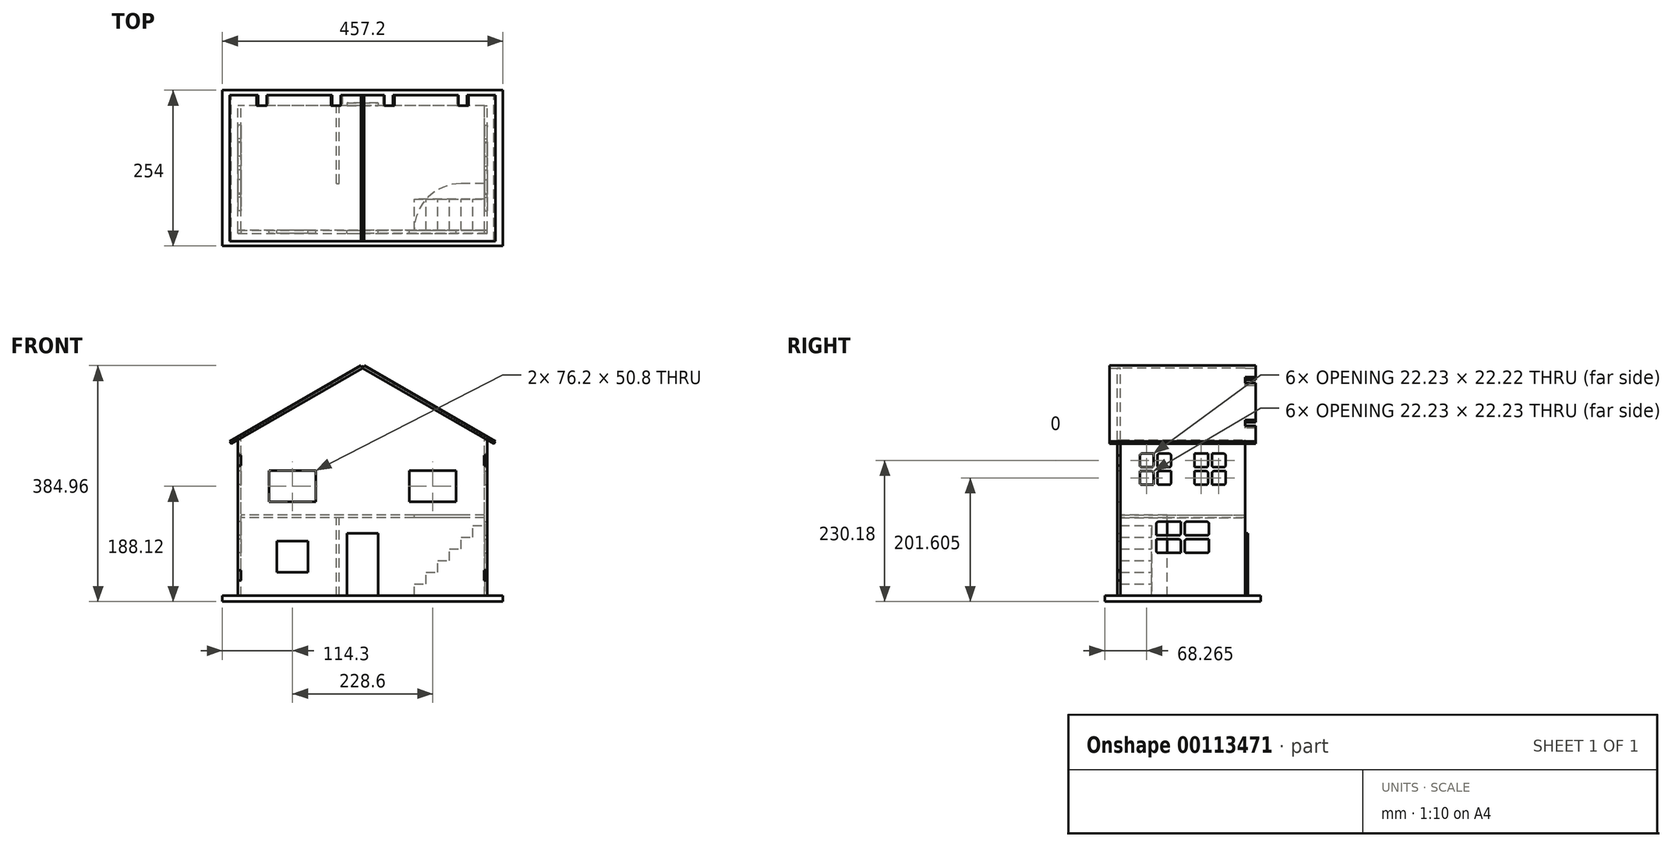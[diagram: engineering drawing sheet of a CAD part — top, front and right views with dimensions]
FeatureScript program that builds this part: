
annotation { "Feature Type Name" : "Feature", "Feature Type Description" : "" }
export const myFeature = defineFeature(function(context is Context, id is Id, definition is map)
    precondition{}
    {
        {
            var Q0;
            Q0=qCreatedBy(makeId("Front.planeOp"),FACE);
            var sketch = newSketch(context, id + "F0", { "sketchPlane" : qUnion([Q0])});
            skLineSegment(sketch, "E0.bottom", {"start": v(-25.4, 0) * mm, "end": v(25.4, 0) * mm});
            skLineSegment(sketch, "E0.top", {"start": v(-25.4, 101.6) * mm, "end": v(25.4, 101.6) * mm});
            skLineSegment(sketch, "E0.left", {"start": v(-25.4, 0) * mm, "end": v(-25.4, 101.6) * mm});
            skLineSegment(sketch, "E0.right", {"start": v(25.4, 0) * mm, "end": v(25.4, 101.6) * mm});
            skLineSegment(sketch, "E1", {"start": v(0, 0) * mm, "end": v(0, -53.95) * mm, "construction": true});
            skLineSegment(sketch, "E2", {"start": v(-203.2, 0) * mm, "end": v(-203.2, 254) * mm});
            skLineSegment(sketch, "E3", {"start": v(-203.2, 254) * mm, "end": v(0, 371.32) * mm});
            skLineSegment(sketch, "E4.MirrorCS", {"start": v(203.2, 0) * mm, "end": v(203.2, 254) * mm});
            skLineSegment(sketch, "E5.MirrorCS", {"start": v(203.2, 254) * mm, "end": v(0, 371.32) * mm});
            skLineSegment(sketch, "E6", {"start": v(-203.2, 0) * mm, "end": v(-25.4, 0) * mm});
            skLineSegment(sketch, "E7", {"start": v(25.4, 0) * mm, "end": v(203.2, 0) * mm});
            skLineSegment(sketch, "E8.bottom", {"start": v(-88.9, 38.1) * mm, "end": v(-139.7, 38.1) * mm});
            skLineSegment(sketch, "E8.top", {"start": v(-88.9, 88.9) * mm, "end": v(-139.7, 88.9) * mm});
            skLineSegment(sketch, "E8.left", {"start": v(-88.9, 38.1) * mm, "end": v(-88.9, 88.9) * mm});
            skLineSegment(sketch, "E8.right", {"start": v(-139.7, 38.1) * mm, "end": v(-139.7, 88.9) * mm});
            skPoint(sketch, "E8.middle", {"position": v(-114.3, 63.5) * mm});
            skLineSegment(sketch, "E9", {"start": v(0, 371.32) * mm, "end": v(-61.92, 371.32) * mm, "construction": true});
            skLineSegment(sketch, "E10.bottom", {"start": v(76.2, 204) * mm, "end": v(152.4, 204) * mm});
            skLineSegment(sketch, "E10.top", {"start": v(76.2, 153.2) * mm, "end": v(152.4, 153.2) * mm});
            skLineSegment(sketch, "E10.left", {"start": v(76.2, 204) * mm, "end": v(76.2, 153.2) * mm});
            skLineSegment(sketch, "E10.right", {"start": v(152.4, 204) * mm, "end": v(152.4, 153.2) * mm});
            skPoint(sketch, "E10.middle", {"position": v(114.3, 178.6) * mm});
            skPoint(sketch, "E11.MirrorP", {"position": v(-114.3, 178.6) * mm});
            skLineSegment(sketch, "E12.MirrorCS", {"start": v(-152.4, 204) * mm, "end": v(-152.4, 153.2) * mm});
            skLineSegment(sketch, "E13.MirrorCS", {"start": v(-76.2, 204) * mm, "end": v(-76.2, 153.2) * mm});
            skLineSegment(sketch, "E14.MirrorCS", {"start": v(-76.2, 153.2) * mm, "end": v(-152.4, 153.2) * mm});
            skLineSegment(sketch, "E15.MirrorCS", {"start": v(-76.2, 204) * mm, "end": v(-152.4, 204) * mm});
            skSolve(sketch);
        }
        {
            var Q0;
            Q0=makeQuery(id+"F0.imprint","IMPRINT",FACE,{"disambiguationData":[TD([[makeQuery(id+"F0.imprint","IMPRINT",EDGE,{"derivedFrom":sQuery(id+"F0.wireOp",EDGE,"E0.top")}),1.0]])]});
            extrude(context, id + "F1", {"entities" : qUnion([Q0]), "depth" : 4.76 * mm});
        }
        {
            var Q0;
            Q0=makeQuery(id+"F1.opExtrude","SWEPT_FACE",FACE,{"disambiguationData":[OSD([sQuery(id+"F0.wireOp",EDGE,"E2")])]});
            var sketch = newSketch(context, id + "F2", { "sketchPlane" : qUnion([Q0])});
            skLineSegment(sketch, "E16.bottom", {"start": v(0, 0) * mm, "end": v(-203.2, 0) * mm});
            skLineSegment(sketch, "E16.top", {"start": v(0, 254) * mm, "end": v(-203.2, 254) * mm});
            skLineSegment(sketch, "E16.left", {"start": v(0, 0) * mm, "end": v(0, 25.4) * mm});
            skLineSegment(sketch, "E16.right", {"start": v(-203.2, 0) * mm, "end": v(-203.2, 25.4) * mm});
            skLineSegment(sketch, "E17.bottom", {"start": v(-144.46, 120.65) * mm, "end": v(-58.74, 120.65) * mm});
            skLineSegment(sketch, "E17.top", {"start": v(-144.46, 69.85) * mm, "end": v(-58.74, 69.85) * mm});
            skLineSegment(sketch, "E17.left", {"start": v(-144.46, 120.65) * mm, "end": v(-144.46, 69.85) * mm});
            skLineSegment(sketch, "E17.right", {"start": v(-58.74, 120.65) * mm, "end": v(-58.74, 69.85) * mm});
            skLineSegment(sketch, "E18", {"start": v(-101.6, 120.65) * mm, "end": v(-101.6, 254) * mm, "construction": true});
            skLineSegment(sketch, "E19.bottom", {"start": v(-120.65, 231.77) * mm, "end": v(-171.45, 231.77) * mm});
            skLineSegment(sketch, "E19.top", {"start": v(-120.65, 180.97) * mm, "end": v(-171.45, 180.97) * mm});
            skLineSegment(sketch, "E19.left", {"start": v(-120.65, 231.77) * mm, "end": v(-120.65, 180.97) * mm});
            skLineSegment(sketch, "E19.right", {"start": v(-171.45, 231.77) * mm, "end": v(-171.45, 180.97) * mm});
            skPoint(sketch, "E19.middle", {"position": v(-146.05, 206.37) * mm});
            skLineSegment(sketch, "E20.MirrorCS", {"start": v(-31.75, 231.77) * mm, "end": v(-31.75, 180.97) * mm});
            skLineSegment(sketch, "E21.MirrorCS", {"start": v(-82.55, 180.97) * mm, "end": v(-31.75, 180.97) * mm});
            skLineSegment(sketch, "E22.MirrorCS", {"start": v(-82.55, 231.77) * mm, "end": v(-82.55, 180.97) * mm});
            skLineSegment(sketch, "E23.MirrorCS", {"start": v(-82.55, 231.77) * mm, "end": v(-31.75, 231.77) * mm});
            skLineSegment(sketch, "E24", {"start": v(-149.22, 231.77) * mm, "end": v(-149.22, 209.55) * mm});
            skLineSegment(sketch, "E25", {"start": v(-149.22, 209.55) * mm, "end": v(-171.45, 209.55) * mm});
            skLineSegment(sketch, "E26", {"start": v(-171.45, 206.37) * mm, "end": v(-146.05, 206.37) * mm, "construction": true});
            skLineSegment(sketch, "E27", {"start": v(-146.05, 206.37) * mm, "end": v(-146.05, 231.77) * mm, "construction": true});
            skLineSegment(sketch, "E28.MirrorCS", {"start": v(-142.88, 209.55) * mm, "end": v(-120.65, 209.55) * mm});
            skLineSegment(sketch, "E29.MirrorCS", {"start": v(-142.88, 231.77) * mm, "end": v(-142.88, 209.55) * mm});
            skLineSegment(sketch, "E30.MirrorCS", {"start": v(-149.22, 203.2) * mm, "end": v(-171.45, 203.2) * mm});
            skLineSegment(sketch, "E31.MirrorCS", {"start": v(-149.22, 180.97) * mm, "end": v(-149.22, 203.2) * mm});
            skLineSegment(sketch, "E32.MirrorCS", {"start": v(-142.88, 180.97) * mm, "end": v(-142.88, 203.2) * mm});
            skLineSegment(sketch, "E33.MirrorCS", {"start": v(-142.88, 203.2) * mm, "end": v(-120.65, 203.2) * mm});
            skLineSegment(sketch, "E34.MirrorCS", {"start": v(-60.33, 231.77) * mm, "end": v(-60.33, 209.55) * mm});
            skLineSegment(sketch, "E35.MirrorCS", {"start": v(-60.33, 203.2) * mm, "end": v(-82.55, 203.2) * mm});
            skLineSegment(sketch, "E36.MirrorCS", {"start": v(-53.98, 231.77) * mm, "end": v(-53.98, 209.55) * mm});
            skLineSegment(sketch, "E37.MirrorCS", {"start": v(-53.98, 209.55) * mm, "end": v(-31.75, 209.55) * mm});
            skLineSegment(sketch, "E38.MirrorCS", {"start": v(-53.98, 203.2) * mm, "end": v(-31.75, 203.2) * mm});
            skLineSegment(sketch, "E39.MirrorCS", {"start": v(-53.98, 180.97) * mm, "end": v(-53.98, 203.2) * mm});
            skLineSegment(sketch, "E40.MirrorCS", {"start": v(-60.33, 209.55) * mm, "end": v(-82.55, 209.55) * mm});
            skLineSegment(sketch, "E41.MirrorCS", {"start": v(-60.33, 180.97) * mm, "end": v(-60.33, 203.2) * mm});
            skLineSegment(sketch, "E42", {"start": v(-104.77, 120.65) * mm, "end": v(-104.77, 98.43) * mm});
            skLineSegment(sketch, "E43", {"start": v(-104.77, 98.43) * mm, "end": v(-144.46, 98.43) * mm});
            skLineSegment(sketch, "E44.MirrorCS", {"start": v(-98.42, 120.65) * mm, "end": v(-98.42, 98.43) * mm});
            skLineSegment(sketch, "E45.MirrorCS", {"start": v(-98.42, 98.43) * mm, "end": v(-58.74, 98.43) * mm});
            skLineSegment(sketch, "E46", {"start": v(-119.08, 95.25) * mm, "end": v(-144.46, 95.25) * mm, "construction": true});
            skLineSegment(sketch, "E47.MirrorCS", {"start": v(-104.77, 92.08) * mm, "end": v(-144.46, 92.08) * mm});
            skLineSegment(sketch, "E48.MirrorCS", {"start": v(-104.77, 69.85) * mm, "end": v(-104.77, 92.08) * mm});
            skLineSegment(sketch, "E49.MirrorCS", {"start": v(-98.42, 69.85) * mm, "end": v(-98.42, 92.08) * mm});
            skLineSegment(sketch, "E50.MirrorCS", {"start": v(-98.42, 92.08) * mm, "end": v(-58.74, 92.08) * mm});
            skLineSegment(sketch, "E51", {"start": v(0, 228.6) * mm, "end": v(4.76, 228.6) * mm});
            skLineSegment(sketch, "E52", {"start": v(4.76, 228.6) * mm, "end": v(4.76, 212.72) * mm});
            skLineSegment(sketch, "E53", {"start": v(4.76, 212.73) * mm, "end": v(0, 212.73) * mm});
            skLineSegment(sketch, "E54", {"start": v(0, 127) * mm, "end": v(28.62, 127) * mm, "construction": true});
            skLineSegment(sketch, "E55.MirrorCS", {"start": v(0, 25.4) * mm, "end": v(4.76, 25.4) * mm});
            skLineSegment(sketch, "E56.MirrorCS", {"start": v(4.76, 25.4) * mm, "end": v(4.76, 41.28) * mm});
            skLineSegment(sketch, "E57.MirrorCS", {"start": v(4.76, 41.27) * mm, "end": v(0, 41.27) * mm});
            skLineSegment(sketch, "E58.trimOffspring", {"start": v(0, 41.27) * mm, "end": v(0, 212.73) * mm});
            skLineSegment(sketch, "E59.trimOffspring", {"start": v(0, 228.6) * mm, "end": v(0, 254) * mm});
            skLineSegment(sketch, "E60.MirrorCS", {"start": v(-207.96, 212.72) * mm, "end": v(-203.2, 212.72) * mm});
            skLineSegment(sketch, "E61.MirrorCS", {"start": v(-207.96, 228.6) * mm, "end": v(-207.96, 212.72) * mm});
            skLineSegment(sketch, "E62.MirrorCS", {"start": v(-203.2, 228.6) * mm, "end": v(-207.96, 228.6) * mm});
            skLineSegment(sketch, "E63.MirrorCS", {"start": v(-203.2, 25.4) * mm, "end": v(-207.96, 25.4) * mm});
            skLineSegment(sketch, "E64.MirrorCS", {"start": v(-207.96, 25.4) * mm, "end": v(-207.96, 41.27) * mm});
            skLineSegment(sketch, "E65.MirrorCS", {"start": v(-207.96, 41.27) * mm, "end": v(-203.2, 41.27) * mm});
            skLineSegment(sketch, "E66.trimOffspring", {"start": v(-203.2, 41.27) * mm, "end": v(-203.2, 212.72) * mm});
            skLineSegment(sketch, "E67.trimOffspring", {"start": v(-203.2, 228.6) * mm, "end": v(-203.2, 254) * mm});
            skSolve(sketch);
        }
        {
            var Q0;
            Q0 = qSketchRegion(id + "F2", true);
            extrude(context, id + "F3", {"entities" : qUnion([Q0]), "oppositeDirection" : true, "depth" : 4.76 * mm});
        }
        {
            var Q0;
            {var subQ6=sQuery(id+"F2.wireOp",EDGE,"E24");Q0=makeQuery(id+"F2.imprint","IMPRINT",FACE,{"disambiguationData":[TD([[makeQuery(id+"F2.imprint","IMPRINT",EDGE,{"derivedFrom":subQ6}),1.0]])]});}
            var Q1;
            {var subQ5=sQuery(id+"F2.wireOp",EDGE,"E34.MirrorCS");Q1=makeQuery(id+"F2.imprint","IMPRINT",FACE,{"disambiguationData":[TD([[makeQuery(id+"F2.imprint","IMPRINT",EDGE,{"derivedFrom":subQ5}),1.0]])]});}
            var Q2;
            {var subQ5=sQuery(id+"F2.wireOp",EDGE,"E42");Q2=makeQuery(id+"F2.imprint","IMPRINT",FACE,{"disambiguationData":[TD([[makeQuery(id+"F2.imprint","IMPRINT",EDGE,{"derivedFrom":subQ5}),1.0]])]});}
            var Q3;
            Q3=makeQuery(id+"F3.opExtrude","CAP_FACE",FACE,{"disambiguationData":[OSD([sQuery(id+"F2.wireOp",EDGE,"E16.bottom"),sQuery(id+"F2.wireOp",EDGE,"E16.top"),sQuery(id+"F2.wireOp",EDGE,"E16.left"),sQuery(id+"F2.wireOp",EDGE,"E16.right"),sQuery(id+"F2.wireOp",EDGE,"E17.bottom"),sQuery(id+"F2.wireOp",EDGE,"E17.top"),sQuery(id+"F2.wireOp",EDGE,"E17.left"),sQuery(id+"F2.wireOp",EDGE,"E17.right"),sQuery(id+"F2.wireOp",EDGE,"E19.bottom"),sQuery(id+"F2.wireOp",EDGE,"E19.top"),sQuery(id+"F2.wireOp",EDGE,"E19.left"),sQuery(id+"F2.wireOp",EDGE,"E19.right"),sQuery(id+"F2.wireOp",EDGE,"E20.MirrorCS"),sQuery(id+"F2.wireOp",EDGE,"E21.MirrorCS"),sQuery(id+"F2.wireOp",EDGE,"E22.MirrorCS"),sQuery(id+"F2.wireOp",EDGE,"E23.MirrorCS")])],"isStart":false});
            extrude(context, id + "F4", {"entities" : qUnion([Q0, Q1, Q2]), "operationType" : NewBodyOperationType.ADD, "endBound" : BoundingType.UP_TO_SURFACE, "oppositeDirection" : true, "endBoundEntityFace" : qUnion([Q3]), "depth" : 25.4 * mm});
        }
        {
            var Q0;
            Q0=makeQuery(id+"F4.opExtrude","SWEPT_EDGE",EDGE,{"disambiguationData":[OSD([sQuery(id+"F2.wireOp",EDGE,"E28.MirrorCS"),sQuery(id+"F2.wireOp",EDGE,"E29.MirrorCS")])]});
            var Q1;
            Q1=makeQuery(id+"F4.opExtrude","SWEPT_EDGE",EDGE,{"disambiguationData":[OSD([sQuery(id+"F2.wireOp",EDGE,"E24"),sQuery(id+"F2.wireOp",EDGE,"E25")])]});
            var Q2;
            Q2=makeQuery(id+"F4.opExtrude","SWEPT_EDGE",EDGE,{"disambiguationData":[OSD([sQuery(id+"F2.wireOp",EDGE,"E19.bottom"),sQuery(id+"F2.wireOp",EDGE,"E24")])]});
            var Q3;
            Q3=makeQuery(id+"F3.opExtrude","SWEPT_EDGE",EDGE,{"disambiguationData":[OSD([sQuery(id+"F2.wireOp",EDGE,"E19.bottom"),sQuery(id+"F2.wireOp",EDGE,"E19.right")])]});
            var Q4;
            Q4=makeQuery(id+"F4.opExtrude","SWEPT_EDGE",EDGE,{"disambiguationData":[OSD([sQuery(id+"F2.wireOp",EDGE,"E19.right"),sQuery(id+"F2.wireOp",EDGE,"E25")])]});
            var Q5;
            Q5=makeQuery(id+"F3.opExtrude","SWEPT_EDGE",EDGE,{"disambiguationData":[OSD([sQuery(id+"F2.wireOp",EDGE,"E19.top"),sQuery(id+"F2.wireOp",EDGE,"E19.right")])]});
            var Q6;
            Q6=makeQuery(id+"F4.opExtrude","SWEPT_EDGE",EDGE,{"disambiguationData":[OSD([sQuery(id+"F2.wireOp",EDGE,"E19.right"),sQuery(id+"F2.wireOp",EDGE,"E30.MirrorCS")])]});
            var Q7;
            Q7=makeQuery(id+"F4.opExtrude","SWEPT_EDGE",EDGE,{"disambiguationData":[OSD([sQuery(id+"F2.wireOp",EDGE,"E19.top"),sQuery(id+"F2.wireOp",EDGE,"E31.MirrorCS")])]});
            var Q8;
            Q8=makeQuery(id+"F4.opExtrude","SWEPT_EDGE",EDGE,{"disambiguationData":[OSD([sQuery(id+"F2.wireOp",EDGE,"E30.MirrorCS"),sQuery(id+"F2.wireOp",EDGE,"E31.MirrorCS")])]});
            var Q9;
            Q9=makeQuery(id+"F4.opExtrude","SWEPT_EDGE",EDGE,{"disambiguationData":[OSD([sQuery(id+"F2.wireOp",EDGE,"E19.left"),sQuery(id+"F2.wireOp",EDGE,"E33.MirrorCS")])]});
            var Q10;
            Q10=makeQuery(id+"F4.opExtrude","SWEPT_EDGE",EDGE,{"disambiguationData":[OSD([sQuery(id+"F2.wireOp",EDGE,"E32.MirrorCS"),sQuery(id+"F2.wireOp",EDGE,"E33.MirrorCS")])]});
            var Q11;
            Q11=makeQuery(id+"F4.opExtrude","SWEPT_EDGE",EDGE,{"disambiguationData":[OSD([sQuery(id+"F2.wireOp",EDGE,"E19.top"),sQuery(id+"F2.wireOp",EDGE,"E32.MirrorCS")])]});
            var Q12;
            Q12=makeQuery(id+"F3.opExtrude","SWEPT_EDGE",EDGE,{"disambiguationData":[OSD([sQuery(id+"F2.wireOp",EDGE,"E19.top"),sQuery(id+"F2.wireOp",EDGE,"E19.left")])]});
            var Q13;
            Q13=makeQuery(id+"F4.opExtrude","SWEPT_EDGE",EDGE,{"disambiguationData":[OSD([sQuery(id+"F2.wireOp",EDGE,"E21.MirrorCS"),sQuery(id+"F2.wireOp",EDGE,"E41.MirrorCS")])]});
            var Q14;
            Q14=makeQuery(id+"F3.opExtrude","SWEPT_EDGE",EDGE,{"disambiguationData":[OSD([sQuery(id+"F2.wireOp",EDGE,"E21.MirrorCS"),sQuery(id+"F2.wireOp",EDGE,"E22.MirrorCS")])]});
            var Q15;
            Q15=makeQuery(id+"F4.opExtrude","SWEPT_EDGE",EDGE,{"disambiguationData":[OSD([sQuery(id+"F2.wireOp",EDGE,"E22.MirrorCS"),sQuery(id+"F2.wireOp",EDGE,"E35.MirrorCS")])]});
            var Q16;
            Q16=makeQuery(id+"F4.opExtrude","SWEPT_EDGE",EDGE,{"disambiguationData":[OSD([sQuery(id+"F2.wireOp",EDGE,"E22.MirrorCS"),sQuery(id+"F2.wireOp",EDGE,"E40.MirrorCS")])]});
            var Q17;
            Q17=makeQuery(id+"F3.opExtrude","SWEPT_EDGE",EDGE,{"disambiguationData":[OSD([sQuery(id+"F2.wireOp",EDGE,"E22.MirrorCS"),sQuery(id+"F2.wireOp",EDGE,"E23.MirrorCS")])]});
            var Q18;
            Q18=makeQuery(id+"F4.opExtrude","SWEPT_EDGE",EDGE,{"disambiguationData":[OSD([sQuery(id+"F2.wireOp",EDGE,"E35.MirrorCS"),sQuery(id+"F2.wireOp",EDGE,"E41.MirrorCS")])]});
            var Q19;
            Q19=makeQuery(id+"F4.opExtrude","SWEPT_EDGE",EDGE,{"disambiguationData":[OSD([sQuery(id+"F2.wireOp",EDGE,"E23.MirrorCS"),sQuery(id+"F2.wireOp",EDGE,"E34.MirrorCS")])]});
            var Q20;
            Q20=makeQuery(id+"F4.opExtrude","SWEPT_EDGE",EDGE,{"disambiguationData":[OSD([sQuery(id+"F2.wireOp",EDGE,"E34.MirrorCS"),sQuery(id+"F2.wireOp",EDGE,"E40.MirrorCS")])]});
            var Q21;
            Q21=makeQuery(id+"F3.opExtrude","SWEPT_EDGE",EDGE,{"disambiguationData":[OSD([sQuery(id+"F2.wireOp",EDGE,"E20.MirrorCS"),sQuery(id+"F2.wireOp",EDGE,"E21.MirrorCS")])]});
            var Q22;
            Q22=makeQuery(id+"F4.opExtrude","SWEPT_EDGE",EDGE,{"disambiguationData":[OSD([sQuery(id+"F2.wireOp",EDGE,"E21.MirrorCS"),sQuery(id+"F2.wireOp",EDGE,"E39.MirrorCS")])]});
            var Q23;
            Q23=makeQuery(id+"F4.opExtrude","SWEPT_EDGE",EDGE,{"disambiguationData":[OSD([sQuery(id+"F2.wireOp",EDGE,"E38.MirrorCS"),sQuery(id+"F2.wireOp",EDGE,"E39.MirrorCS")])]});
            var Q24;
            Q24=makeQuery(id+"F4.opExtrude","SWEPT_EDGE",EDGE,{"disambiguationData":[OSD([sQuery(id+"F2.wireOp",EDGE,"E20.MirrorCS"),sQuery(id+"F2.wireOp",EDGE,"E38.MirrorCS")])]});
            var Q25;
            Q25=makeQuery(id+"F3.opExtrude","SWEPT_EDGE",EDGE,{"disambiguationData":[OSD([sQuery(id+"F2.wireOp",EDGE,"E20.MirrorCS"),sQuery(id+"F2.wireOp",EDGE,"E23.MirrorCS")])]});
            var Q26;
            Q26=makeQuery(id+"F4.opExtrude","SWEPT_EDGE",EDGE,{"disambiguationData":[OSD([sQuery(id+"F2.wireOp",EDGE,"E23.MirrorCS"),sQuery(id+"F2.wireOp",EDGE,"E36.MirrorCS")])]});
            var Q27;
            Q27=makeQuery(id+"F4.opExtrude","SWEPT_EDGE",EDGE,{"disambiguationData":[OSD([sQuery(id+"F2.wireOp",EDGE,"E20.MirrorCS"),sQuery(id+"F2.wireOp",EDGE,"E37.MirrorCS")])]});
            var Q28;
            Q28=makeQuery(id+"F4.opExtrude","SWEPT_EDGE",EDGE,{"disambiguationData":[OSD([sQuery(id+"F2.wireOp",EDGE,"E36.MirrorCS"),sQuery(id+"F2.wireOp",EDGE,"E37.MirrorCS")])]});
            var Q29;
            Q29=makeQuery(id+"F3.opExtrude","SWEPT_EDGE",EDGE,{"disambiguationData":[OSD([sQuery(id+"F2.wireOp",EDGE,"E17.top"),sQuery(id+"F2.wireOp",EDGE,"E17.left")])]});
            var Q30;
            Q30=makeQuery(id+"F4.opExtrude","SWEPT_EDGE",EDGE,{"disambiguationData":[OSD([sQuery(id+"F2.wireOp",EDGE,"E17.top"),sQuery(id+"F2.wireOp",EDGE,"E49.MirrorCS")])]});
            var Q31;
            Q31=makeQuery(id+"F4.opExtrude","SWEPT_EDGE",EDGE,{"disambiguationData":[OSD([sQuery(id+"F2.wireOp",EDGE,"E44.MirrorCS"),sQuery(id+"F2.wireOp",EDGE,"E45.MirrorCS")])]});
            var Q32;
            Q32=makeQuery(id+"F4.opExtrude","SWEPT_EDGE",EDGE,{"disambiguationData":[OSD([sQuery(id+"F2.wireOp",EDGE,"E17.left"),sQuery(id+"F2.wireOp",EDGE,"E43")])]});
            var Q33;
            Q33=makeQuery(id+"F4.opExtrude","SWEPT_EDGE",EDGE,{"disambiguationData":[OSD([sQuery(id+"F2.wireOp",EDGE,"E49.MirrorCS"),sQuery(id+"F2.wireOp",EDGE,"E50.MirrorCS")])]});
            var Q34;
            Q34=makeQuery(id+"F3.opExtrude","SWEPT_EDGE",EDGE,{"disambiguationData":[OSD([sQuery(id+"F2.wireOp",EDGE,"E17.bottom"),sQuery(id+"F2.wireOp",EDGE,"E17.left")])]});
            var Q35;
            Q35=makeQuery(id+"F4.opExtrude","SWEPT_EDGE",EDGE,{"disambiguationData":[OSD([sQuery(id+"F2.wireOp",EDGE,"E17.bottom"),sQuery(id+"F2.wireOp",EDGE,"E42")])]});
            var Q36;
            Q36=makeQuery(id+"F3.opExtrude","SWEPT_EDGE",EDGE,{"disambiguationData":[OSD([sQuery(id+"F2.wireOp",EDGE,"E17.bottom"),sQuery(id+"F2.wireOp",EDGE,"E17.right")])]});
            var Q37;
            Q37=makeQuery(id+"F4.opExtrude","SWEPT_EDGE",EDGE,{"disambiguationData":[OSD([sQuery(id+"F2.wireOp",EDGE,"E17.bottom"),sQuery(id+"F2.wireOp",EDGE,"E44.MirrorCS")])]});
            var Q38;
            Q38=makeQuery(id+"F4.opExtrude","SWEPT_EDGE",EDGE,{"disambiguationData":[OSD([sQuery(id+"F2.wireOp",EDGE,"E17.right"),sQuery(id+"F2.wireOp",EDGE,"E50.MirrorCS")])]});
            var Q39;
            Q39=makeQuery(id+"F4.opExtrude","SWEPT_EDGE",EDGE,{"disambiguationData":[OSD([sQuery(id+"F2.wireOp",EDGE,"E47.MirrorCS"),sQuery(id+"F2.wireOp",EDGE,"E48.MirrorCS")])]});
            var Q40;
            Q40=makeQuery(id+"F4.opExtrude","SWEPT_EDGE",EDGE,{"disambiguationData":[OSD([sQuery(id+"F2.wireOp",EDGE,"E42"),sQuery(id+"F2.wireOp",EDGE,"E43")])]});
            var Q41;
            Q41=makeQuery(id+"F3.opExtrude","SWEPT_EDGE",EDGE,{"disambiguationData":[OSD([sQuery(id+"F2.wireOp",EDGE,"E17.top"),sQuery(id+"F2.wireOp",EDGE,"E17.right")])]});
            var Q42;
            Q42=makeQuery(id+"F4.opExtrude","SWEPT_EDGE",EDGE,{"disambiguationData":[OSD([sQuery(id+"F2.wireOp",EDGE,"E17.top"),sQuery(id+"F2.wireOp",EDGE,"E48.MirrorCS")])]});
            var Q43;
            Q43=makeQuery(id+"F4.opExtrude","SWEPT_EDGE",EDGE,{"disambiguationData":[OSD([sQuery(id+"F2.wireOp",EDGE,"E17.left"),sQuery(id+"F2.wireOp",EDGE,"E47.MirrorCS")])]});
            fillet(context, id + "F5", {"entities" : qUnion([Q0, Q1, Q2, Q3, Q4, Q5, Q6, Q7, Q8, Q9, Q10, Q11, Q12, Q13, Q14, Q15, Q16, Q17, Q18, Q19, Q20, Q21, Q22, Q23, Q24, Q25, Q26, Q27, Q28, Q29, Q30, Q31, Q32, Q33, Q34, Q35, Q36, Q37, Q38, Q39, Q40, Q41, Q42, Q43]), "radius" : 3.17 * mm, "tangentPropagation" : true, "allowEdgeOverflow" : false});
        }
        {
            var Q0;
            Q0=makeQuery(id+"F10.opExtrude","SWEPT_BODY",BODY,{"disambiguationData":[OSD([sQuery(id+"F9.wireOp",EDGE,"E75.bottom"),sQuery(id+"F9.wireOp",EDGE,"E75.top"),sQuery(id+"F9.wireOp",EDGE,"E75.left"),sQuery(id+"F9.wireOp",EDGE,"E75.right")])]});
            var Q1;
            Q1=makeQuery(id+"F3.opExtrude","SWEPT_BODY",BODY,{"disambiguationData":[OSD([sQuery(id+"F2.wireOp",EDGE,"E16.bottom"),sQuery(id+"F2.wireOp",EDGE,"E16.top"),sQuery(id+"F2.wireOp",EDGE,"E16.left"),sQuery(id+"F2.wireOp",EDGE,"E16.right"),sQuery(id+"F2.wireOp",EDGE,"E17.bottom"),sQuery(id+"F2.wireOp",EDGE,"E17.top"),sQuery(id+"F2.wireOp",EDGE,"E17.left"),sQuery(id+"F2.wireOp",EDGE,"E17.right")])]});
            var Q2;
            Q2=qCreatedBy(makeId("Right.planeOp"),FACE);
            mirror(context, id + "F6", {"entities" : qUnion([Q0, Q1]), "mirrorPlane" : qUnion([Q2])});
        }
        {
            var Q0;
            Q0=makeQuery(id+"F6.opPattern","COPY",FACE,{"derivedFrom":makeQuery(id+"F3.opExtrude","SWEPT_FACE",FACE,{"disambiguationData":[OSD([sQuery(id+"F2.wireOp",EDGE,"E16.right")])]}),"instanceName":"1"});
            var sketch = newSketch(context, id + "F7", { "sketchPlane" : qUnion([Q0])});
            skLineSegment(sketch, "E68.right", {"start": v(203.2, 0) * mm, "end": v(203.2, 254) * mm});
            skLineSegment(sketch, "E69", {"start": v(0, 371.32) * mm, "end": v(203.2, 254) * mm});
            skLineSegment(sketch, "E70.bottom", {"start": v(-63.5, 234.95) * mm, "end": v(63.5, 234.95) * mm});
            skLineSegment(sketch, "E70.top", {"start": v(-63.5, 184.15) * mm, "end": v(63.5, 184.15) * mm});
            skLineSegment(sketch, "E70.left", {"start": v(-63.5, 234.95) * mm, "end": v(-63.5, 184.15) * mm});
            skLineSegment(sketch, "E70.right", {"start": v(63.5, 234.95) * mm, "end": v(63.5, 184.15) * mm});
            skLineSegment(sketch, "E71", {"start": v(0, 0) * mm, "end": v(0, 184.15) * mm, "construction": true});
            skLineSegment(sketch, "E72", {"start": v(203.2, 0) * mm, "end": v(-203.2, 0) * mm});
            skLineSegment(sketch, "E73", {"start": v(-203.2, 0) * mm, "end": v(-203.2, 254) * mm});
            skLineSegment(sketch, "E74", {"start": v(-203.2, 254) * mm, "end": v(0, 371.32) * mm});
            skSolve(sketch);
        }
        {
            var Q0;
            Q0 = qSketchRegion(id + "F7", true);
            extrude(context, id + "F8", {"entities" : qUnion([Q0]), "depth" : 4.76 * mm});
        }
        {
            var Q0;
            Q0=makeQuery(id+"F1.opExtrude","SWEPT_FACE",FACE,{"disambiguationData":[OSD([sQuery(id+"F0.wireOp",EDGE,"E3")])]});
            var sketch = newSketch(context, id + "F9", { "sketchPlane" : qUnion([Q0])});
            skLineSegment(sketch, "E75.bottom", {"start": v(185.66, -17.46) * mm, "end": v(-61.68, -17.46) * mm});
            skLineSegment(sketch, "E75.top", {"start": v(185.66, 220.66) * mm, "end": v(-61.68, 220.66) * mm});
            skLineSegment(sketch, "E75.left", {"start": v(185.66, -17.46) * mm, "end": v(185.66, 220.66) * mm});
            skLineSegment(sketch, "E75.right", {"start": v(-61.68, -17.46) * mm, "end": v(-61.68, 220.66) * mm});
            skSolve(sketch);
        }
        {
            var Q0;
            Q0 = qSketchRegion(id + "F9", true);
            extrude(context, id + "F10", {"entities" : qUnion([Q0]), "depth" : 4.76 * mm});
        }
        {
            var Q0;
            Q0=makeQuery(id+"F10.opExtrude","SWEPT_BODY",BODY,{"disambiguationData":[OSD([sQuery(id+"F9.wireOp",EDGE,"E75.bottom"),sQuery(id+"F9.wireOp",EDGE,"E75.top"),sQuery(id+"F9.wireOp",EDGE,"E75.left"),sQuery(id+"F9.wireOp",EDGE,"E75.right")])]});
            var Q1;
            Q1=qCreatedBy(makeId("Right.planeOp"),FACE);
            mirror(context, id + "F11", {"entities" : qUnion([Q0]), "mirrorPlane" : qUnion([Q1])});
        }
        {
            var Q0;
            Q0=qCreatedBy(makeId("Top.planeOp"),FACE);
            var sketch = newSketch(context, id + "F12", { "sketchPlane" : qUnion([Q0])});
            skLineSegment(sketch, "E76.bottom", {"start": v(-228.6, -25.4) * mm, "end": v(228.6, -25.4) * mm});
            skLineSegment(sketch, "E76.top", {"start": v(-228.6, 228.6) * mm, "end": v(228.6, 228.6) * mm});
            skLineSegment(sketch, "E76.left", {"start": v(-228.6, -25.4) * mm, "end": v(-228.6, 228.6) * mm});
            skLineSegment(sketch, "E76.right", {"start": v(228.6, -25.4) * mm, "end": v(228.6, 228.6) * mm});
            skLineSegment(sketch, "E77", {"start": v(0, 0) * mm, "end": v(0, -25.4) * mm, "construction": true});
            skLineSegment(sketch, "E78", {"start": v(-228.6, 101.6) * mm, "end": v(-198.44, 101.6) * mm, "construction": true});
            skSolve(sketch);
        }
        {
            var Q0;
            Q0 = qSketchRegion(id + "F12", true);
            extrude(context, id + "F13", {"entities" : qUnion([Q0]), "oppositeDirection" : true, "offsetDistance" : 25.4 * mm, "depth" : 9.52 * mm});
        }
        {
            var Q0;
            Q0=qCreatedBy(makeId("Top.planeOp"),FACE);
            cPlane(context, id + "F14", {"entities" : qUnion([Q0]), "cplaneType" : CPlaneType.OFFSET, "offset" : 127 * mm, "width" : 152.4 * mm, "height" : 152.4 * mm});
        }
        {
            var Q0;
            Q0=qCreatedBy(id+"F14.planeOp",FACE);
            var sketch = newSketch(context, id + "F15", { "sketchPlane" : qUnion([Q0])});
            skLineSegment(sketch, "E79.bottom", {"start": v(198.44, 0) * mm, "end": v(-198.44, 0) * mm});
            skLineSegment(sketch, "E79.top", {"start": v(198.44, 203.2) * mm, "end": v(-198.44, 203.2) * mm});
            skLineSegment(sketch, "E79.left", {"start": v(198.44, 0) * mm, "end": v(198.44, 203.2) * mm});
            skLineSegment(sketch, "E79.right", {"start": v(-198.44, 0) * mm, "end": v(-198.44, 203.2) * mm});
            skSolve(sketch);
        }
        {
            var Q0;
            Q0 = qSketchRegion(id + "F15", true);
            extrude(context, id + "F16", {"entities" : qUnion([Q0]), "depth" : 4.76 * mm});
        }
        {
            var Q0;
            Q0=makeQuery(id+"F16.opExtrude","CAP_FACE",FACE,{"disambiguationData":[OSD([sQuery(id+"F15.wireOp",EDGE,"E79.bottom"),sQuery(id+"F15.wireOp",EDGE,"E79.top"),sQuery(id+"F15.wireOp",EDGE,"E79.left"),sQuery(id+"F15.wireOp",EDGE,"E79.right")])],"isStart":false});
            var sketch = newSketch(context, id + "F17", { "sketchPlane" : qUnion([Q0])});
            skLineSegment(sketch, "E80", {"start": v(198.44, 76.2) * mm, "end": v(198.44, 0) * mm});
            skLineSegment(sketch, "E81", {"start": v(198.44, 76.2) * mm, "end": v(160.34, 76.2) * mm});
            skArc(sketch, "E82", {"start": v(160.34, 76.2) * mm, "mid": v(106.46, 53.88) * mm, "end": v(84.14, 0) * mm});
            skLineSegment(sketch, "E83", {"start": v(198.44, 0) * mm, "end": v(84.14, 0) * mm});
            skSolve(sketch);
        }
        {
            var Q0;
            {var subQ0=sQuery(id+"F17.wireOp",EDGE,"lvDJLR7u-k1KV-GbFS-caSa-MnMNnrSgLqYe");Q0=makeQuery(id+"F17.imprint","IMPRINT",FACE,{"disambiguationData":[TD([[makeQuery(id+"F17.imprint","IMPRINT",EDGE,{"derivedFrom":subQ0}),-1.0]])]});}
            var Q1;
            Q1=makeQuery(id+"F17.imprint","IMPRINT",FACE,{"disambiguationData":[TD([[makeQuery(id+"F17.imprint","IMPRINT",EDGE,{"derivedFrom":sQuery(id+"F17.wireOp",EDGE,"E80")}),1.0]])]});
            var Q2;
            Q2=makeQuery(id+"F16.opExtrude","CAP_FACE",FACE,{"disambiguationData":[OSD([sQuery(id+"F15.wireOp",EDGE,"E79.bottom"),sQuery(id+"F15.wireOp",EDGE,"E79.top"),sQuery(id+"F15.wireOp",EDGE,"E79.left"),sQuery(id+"F15.wireOp",EDGE,"E79.right")])],"isStart":true});
            extrude(context, id + "F18", {"entities" : qUnion([Q0, Q1]), "operationType" : NewBodyOperationType.REMOVE, "oppositeDirection" : true, "endBoundEntityFace" : qUnion([Q2]), "depth" : 4.76 * mm});
        }
        {
            var Q0;
            Q0=qCreatedBy(makeId("Front.planeOp"),FACE);
            cPlane(context, id + "F19", {"entities" : qUnion([Q0]), "cplaneType" : CPlaneType.OFFSET, "offset" : 50.8 * mm, "oppositeDirection" : true, "width" : 152.4 * mm, "height" : 152.4 * mm});
        }
        {
            var Q0;
            Q0=qCreatedBy(id+"F19.planeOp",FACE);
            var sketch = newSketch(context, id + "F20", { "sketchPlane" : qUnion([Q0])});
            skLineSegment(sketch, "E84", {"start": v(84.14, 0) * mm, "end": v(84.14, 19.05) * mm});
            skLineSegment(sketch, "E85", {"start": v(84.14, 19.05) * mm, "end": v(103.19, 19.05) * mm});
            skLineSegment(sketch, "E86", {"start": v(103.19, 19.05) * mm, "end": v(103.19, 38.1) * mm});
            skLineSegment(sketch, "E87", {"start": v(103.19, 38.1) * mm, "end": v(122.24, 38.1) * mm});
            skLineSegment(sketch, "E88", {"start": v(122.24, 38.1) * mm, "end": v(122.24, 57.15) * mm});
            skLineSegment(sketch, "E89", {"start": v(122.24, 57.15) * mm, "end": v(141.29, 57.15) * mm});
            skLineSegment(sketch, "E90", {"start": v(141.29, 57.15) * mm, "end": v(141.29, 76.2) * mm});
            skLineSegment(sketch, "E91", {"start": v(141.29, 76.2) * mm, "end": v(160.34, 76.2) * mm});
            skLineSegment(sketch, "E92", {"start": v(160.34, 76.2) * mm, "end": v(160.34, 95.25) * mm});
            skLineSegment(sketch, "E93", {"start": v(160.34, 95.25) * mm, "end": v(179.39, 95.25) * mm});
            skLineSegment(sketch, "E94", {"start": v(179.39, 95.25) * mm, "end": v(179.39, 114.3) * mm});
            skLineSegment(sketch, "E95", {"start": v(179.39, 114.3) * mm, "end": v(198.44, 114.3) * mm});
            skLineSegment(sketch, "E96", {"start": v(198.44, 114.3) * mm, "end": v(198.44, 0) * mm});
            skLineSegment(sketch, "E97", {"start": v(198.44, 0) * mm, "end": v(84.14, 0) * mm});
            skSolve(sketch);
        }
        {
            var Q0;
            Q0 = qSketchRegion(id + "F20", true);
            extrude(context, id + "F21", {"entities" : qUnion([Q0]), "depth" : 50.8 * mm});
        }
        {
            var Q0;
            Q0=makeQuery(id+"F16.opExtrude","CAP_FACE",FACE,{"disambiguationData":[OSD([sQuery(id+"F15.wireOp",EDGE,"E79.bottom"),sQuery(id+"F15.wireOp",EDGE,"E79.top"),sQuery(id+"F15.wireOp",EDGE,"E79.left"),sQuery(id+"F15.wireOp",EDGE,"E79.right")])],"isStart":true});
            var sketch = newSketch(context, id + "F22", { "sketchPlane" : qUnion([Q0])});
            skLineSegment(sketch, "E98.bottom", {"start": v(-38.1, -203.2) * mm, "end": v(-42.86, -203.2) * mm});
            skLineSegment(sketch, "E98.top", {"start": v(-38.1, -76.2) * mm, "end": v(-42.86, -76.2) * mm});
            skLineSegment(sketch, "E98.left", {"start": v(-38.1, -203.2) * mm, "end": v(-38.1, -76.2) * mm});
            skLineSegment(sketch, "E98.right", {"start": v(-42.86, -203.2) * mm, "end": v(-42.86, -76.2) * mm});
            skSolve(sketch);
        }
        {
            var Q0;
            Q0 = qSketchRegion(id + "F22", true);
            extrude(context, id + "F23", {"entities" : qUnion([Q0]), "endBound" : BoundingType.UP_TO_NEXT, "depth" : 25.4 * mm, "offsetDistance" : 25.4 * mm});
        }
        {
            var Q0;
            Q0=makeQuery(id+"F1.opExtrude","CAP_FACE",FACE,{"disambiguationData":[OSD([sQuery(id+"F0.wireOp",EDGE,"E0.top"),sQuery(id+"F0.wireOp",EDGE,"E0.left"),sQuery(id+"F0.wireOp",EDGE,"E0.right"),sQuery(id+"F0.wireOp",EDGE,"E2"),sQuery(id+"F0.wireOp",EDGE,"E3"),sQuery(id+"F0.wireOp",EDGE,"E4.MirrorCS"),sQuery(id+"F0.wireOp",EDGE,"E5.MirrorCS"),sQuery(id+"F0.wireOp",EDGE,"E6"),sQuery(id+"F0.wireOp",EDGE,"E7"),sQuery(id+"F0.wireOp",EDGE,"E8.bottom"),sQuery(id+"F0.wireOp",EDGE,"E8.top"),sQuery(id+"F0.wireOp",EDGE,"E8.left"),sQuery(id+"F0.wireOp",EDGE,"E8.right"),sQuery(id+"F0.wireOp",EDGE,"E10.bottom"),sQuery(id+"F0.wireOp",EDGE,"E10.top"),sQuery(id+"F0.wireOp",EDGE,"E10.left"),sQuery(id+"F0.wireOp",EDGE,"E10.right"),sQuery(id+"F0.wireOp",EDGE,"E12.MirrorCS"),sQuery(id+"F0.wireOp",EDGE,"E13.MirrorCS"),sQuery(id+"F0.wireOp",EDGE,"E14.MirrorCS"),sQuery(id+"F0.wireOp",EDGE,"E15.MirrorCS")])],"isStart":false});
            var sketch = newSketch(context, id + "F24", { "sketchPlane" : qUnion([Q0])});
            skLineSegment(sketch, "E99.bottom", {"start": v(-198.04, 212.33) * mm, "end": v(-203.2, 212.33) * mm});
            skLineSegment(sketch, "E99.top", {"start": v(-198.04, 229) * mm, "end": v(-203.2, 229) * mm});
            skLineSegment(sketch, "E99.left", {"start": v(-198.04, 212.33) * mm, "end": v(-198.04, 229) * mm});
            skLineSegment(sketch, "E99.right", {"start": v(-203.2, 212.33) * mm, "end": v(-203.2, 229) * mm});
            skLineSegment(sketch, "E100", {"start": v(-198.04, 220.66) * mm, "end": v(-203.2, 220.66) * mm, "construction": true});
            skLineSegment(sketch, "E101", {"start": v(-198.44, 220.66) * mm, "end": v(-198.04, 220.66) * mm});
            skLineSegment(sketch, "E102", {"start": v(-203.2, 127) * mm, "end": v(-179.7, 127) * mm, "construction": true});
            skLineSegment(sketch, "E103.MirrorCS", {"start": v(-203.2, 41.67) * mm, "end": v(-203.2, 25) * mm});
            skLineSegment(sketch, "E104.MirrorCS", {"start": v(-198.04, 25) * mm, "end": v(-203.2, 25) * mm});
            skLineSegment(sketch, "E105.MirrorCS", {"start": v(-198.04, 41.67) * mm, "end": v(-198.04, 25) * mm});
            skLineSegment(sketch, "E106.MirrorCS", {"start": v(-198.04, 41.67) * mm, "end": v(-203.2, 41.67) * mm});
            skLineSegment(sketch, "E107", {"start": v(0, 130.59) * mm, "end": v(0, 263.98) * mm, "construction": true});
            skLineSegment(sketch, "E108.MirrorCS", {"start": v(198.04, 229) * mm, "end": v(203.2, 229) * mm});
            skLineSegment(sketch, "E109.MirrorCS", {"start": v(198.04, 212.33) * mm, "end": v(198.04, 229) * mm});
            skLineSegment(sketch, "E110.MirrorCS", {"start": v(203.2, 212.33) * mm, "end": v(203.2, 229) * mm});
            skLineSegment(sketch, "E111.MirrorCS", {"start": v(198.04, 212.33) * mm, "end": v(203.2, 212.33) * mm});
            skLineSegment(sketch, "E112.MirrorCS", {"start": v(198.04, 25) * mm, "end": v(203.2, 25) * mm});
            skLineSegment(sketch, "E113.MirrorCS", {"start": v(198.04, 41.67) * mm, "end": v(198.04, 25) * mm});
            skLineSegment(sketch, "E114.MirrorCS", {"start": v(203.2, 41.67) * mm, "end": v(203.2, 25) * mm});
            skLineSegment(sketch, "E115.MirrorCS", {"start": v(198.04, 41.67) * mm, "end": v(203.2, 41.67) * mm});
            skSolve(sketch);
        }
        {
            var Q0;
            Q0 = qSketchRegion(id + "F24", true);
            extrude(context, id + "F25", {"entities" : qUnion([Q0]), "operationType" : NewBodyOperationType.REMOVE, "endBound" : BoundingType.UP_TO_NEXT, "oppositeDirection" : true, "depth" : 25.4 * mm, "offsetDistance" : 25.4 * mm});
        }
        {
            var Q0;
            Q0=makeQuery(id+"F1.opExtrude","CAP_FACE",FACE,{"disambiguationData":[OSD([sQuery(id+"F0.wireOp",EDGE,"E0.top"),sQuery(id+"F0.wireOp",EDGE,"E0.left"),sQuery(id+"F0.wireOp",EDGE,"E0.right"),sQuery(id+"F0.wireOp",EDGE,"E2"),sQuery(id+"F0.wireOp",EDGE,"E3"),sQuery(id+"F0.wireOp",EDGE,"E4.MirrorCS"),sQuery(id+"F0.wireOp",EDGE,"E5.MirrorCS"),sQuery(id+"F0.wireOp",EDGE,"E6"),sQuery(id+"F0.wireOp",EDGE,"E7"),sQuery(id+"F0.wireOp",EDGE,"E8.bottom"),sQuery(id+"F0.wireOp",EDGE,"E8.top"),sQuery(id+"F0.wireOp",EDGE,"E8.left"),sQuery(id+"F0.wireOp",EDGE,"E8.right"),sQuery(id+"F0.wireOp",EDGE,"E10.bottom"),sQuery(id+"F0.wireOp",EDGE,"E10.top"),sQuery(id+"F0.wireOp",EDGE,"E10.left"),sQuery(id+"F0.wireOp",EDGE,"E10.right"),sQuery(id+"F0.wireOp",EDGE,"E12.MirrorCS"),sQuery(id+"F0.wireOp",EDGE,"E13.MirrorCS"),sQuery(id+"F0.wireOp",EDGE,"E14.MirrorCS"),sQuery(id+"F0.wireOp",EDGE,"E15.MirrorCS")])],"isStart":false});
            var sketch = newSketch(context, id + "F26", { "sketchPlane" : qUnion([Q0])});
            skLineSegment(sketch, "E116", {"start": v(-170.2, 273.05) * mm, "end": v(-172.59, 277.17) * mm});
            skLineSegment(sketch, "E117", {"start": v(-172.59, 277.17) * mm, "end": v(-156.09, 286.7) * mm});
            skLineSegment(sketch, "E118", {"start": v(-156.09, 286.7) * mm, "end": v(-153.7, 282.58) * mm});
            skLineSegment(sketch, "E119", {"start": v(-153.7, 282.58) * mm, "end": v(-170.2, 273.05) * mm});
            skLineSegment(sketch, "E120", {"start": v(-49.5, 342.74) * mm, "end": v(-51.87, 346.87) * mm});
            skLineSegment(sketch, "E121", {"start": v(-51.87, 346.87) * mm, "end": v(-35.38, 356.4) * mm});
            skLineSegment(sketch, "E122", {"start": v(-35.38, 356.4) * mm, "end": v(-33, 352.27) * mm});
            skLineSegment(sketch, "E123", {"start": v(-33, 352.27) * mm, "end": v(-49.5, 342.74) * mm});
            skLineSegment(sketch, "E124", {"start": v(0, 0) * mm, "end": v(0, 391.53) * mm, "construction": true});
            skLineSegment(sketch, "E125.MirrorCS", {"start": v(49.5, 342.74) * mm, "end": v(51.87, 346.87) * mm});
            skLineSegment(sketch, "E126.MirrorCS", {"start": v(51.87, 346.87) * mm, "end": v(35.38, 356.4) * mm});
            skLineSegment(sketch, "E127.MirrorCS", {"start": v(35.38, 356.4) * mm, "end": v(33, 352.27) * mm});
            skLineSegment(sketch, "E128.MirrorCS", {"start": v(33, 352.27) * mm, "end": v(49.5, 342.74) * mm});
            skLineSegment(sketch, "E129.MirrorCS", {"start": v(172.59, 277.17) * mm, "end": v(156.09, 286.7) * mm});
            skLineSegment(sketch, "E130.MirrorCS", {"start": v(170.2, 273.05) * mm, "end": v(172.59, 277.17) * mm});
            skLineSegment(sketch, "E131.MirrorCS", {"start": v(156.09, 286.7) * mm, "end": v(153.7, 282.58) * mm});
            skLineSegment(sketch, "E132.MirrorCS", {"start": v(153.7, 282.58) * mm, "end": v(170.2, 273.05) * mm});
            skSolve(sketch);
        }
        {
            var Q0;
            Q0 = qSketchRegion(id + "F26", true);
            var Q1;
            Q1=makeQuery(id+"F1.opExtrude","CAP_FACE",FACE,{"disambiguationData":[OSD([sQuery(id+"F0.wireOp",EDGE,"E0.top"),sQuery(id+"F0.wireOp",EDGE,"E0.left"),sQuery(id+"F0.wireOp",EDGE,"E0.right"),sQuery(id+"F0.wireOp",EDGE,"E2"),sQuery(id+"F0.wireOp",EDGE,"E3"),sQuery(id+"F0.wireOp",EDGE,"E4.MirrorCS"),sQuery(id+"F0.wireOp",EDGE,"E5.MirrorCS"),sQuery(id+"F0.wireOp",EDGE,"E6"),sQuery(id+"F0.wireOp",EDGE,"E7"),sQuery(id+"F0.wireOp",EDGE,"E8.bottom"),sQuery(id+"F0.wireOp",EDGE,"E8.top"),sQuery(id+"F0.wireOp",EDGE,"E8.left"),sQuery(id+"F0.wireOp",EDGE,"E8.right"),sQuery(id+"F0.wireOp",EDGE,"E10.bottom"),sQuery(id+"F0.wireOp",EDGE,"E10.top"),sQuery(id+"F0.wireOp",EDGE,"E10.left"),sQuery(id+"F0.wireOp",EDGE,"E10.right"),sQuery(id+"F0.wireOp",EDGE,"E12.MirrorCS"),sQuery(id+"F0.wireOp",EDGE,"E13.MirrorCS"),sQuery(id+"F0.wireOp",EDGE,"E14.MirrorCS"),sQuery(id+"F0.wireOp",EDGE,"E15.MirrorCS")])],"isStart":true});
            extrude(context, id + "F27", {"entities" : qUnion([Q0]), "operationType" : NewBodyOperationType.ADD, "endBound" : BoundingType.UP_TO_SURFACE, "oppositeDirection" : true, "depth" : 25.4 * mm, "endBoundEntityFace" : qUnion([Q1]), "offsetDistance" : 25.4 * mm});
        }
        {
            var Q0;
            Q0=makeQuery(id+"F8.opExtrude","CAP_FACE",FACE,{"disambiguationData":[OSD([sQuery(id+"F7.wireOp",EDGE,"E68.right"),sQuery(id+"F7.wireOp",EDGE,"E69"),sQuery(id+"F7.wireOp",EDGE,"E70.bottom"),sQuery(id+"F7.wireOp",EDGE,"E70.top"),sQuery(id+"F7.wireOp",EDGE,"E70.left"),sQuery(id+"F7.wireOp",EDGE,"E70.right"),sQuery(id+"F7.wireOp",EDGE,"E72"),sQuery(id+"F7.wireOp",EDGE,"E73"),sQuery(id+"F7.wireOp",EDGE,"E74")])],"isStart":true});
            var sketch = newSketch(context, id + "F28", { "sketchPlane" : qUnion([Q0])});
            skLineSegment(sketch, "E133.0", {"start": v(198.04, 212.33) * mm, "end": v(198.04, 229) * mm});
            skLineSegment(sketch, "E133.1", {"start": v(198.04, 229) * mm, "end": v(203.2, 229) * mm});
            skLineSegment(sketch, "E133.2", {"start": v(198.04, 212.33) * mm, "end": v(203.2, 212.33) * mm});
            skLineSegment(sketch, "E134.0", {"start": v(198.04, 41.67) * mm, "end": v(198.04, 25) * mm});
            skLineSegment(sketch, "E134.1.0", {"start": v(198.04, 25) * mm, "end": v(198.04, 41.67) * mm});
            skLineSegment(sketch, "E134.1.1", {"start": v(198.04, 41.67) * mm, "end": v(203.2, 41.67) * mm});
            skLineSegment(sketch, "E134.1.2", {"start": v(203.2, 41.67) * mm, "end": v(203.2, 212.33) * mm});
            skLineSegment(sketch, "E134.1.3", {"start": v(203.2, 212.33) * mm, "end": v(198.04, 212.33) * mm});
            skLineSegment(sketch, "E134.1.6", {"start": v(203.2, 229) * mm, "end": v(203.2, 254) * mm});
            skLineSegment(sketch, "E134.1.7", {"start": v(203.2, 254) * mm, "end": v(170.2, 273.05) * mm});
            skLineSegment(sketch, "E134.1.8", {"start": v(170.2, 273.05) * mm, "end": v(172.59, 277.17) * mm});
            skLineSegment(sketch, "E134.1.9", {"start": v(172.59, 277.17) * mm, "end": v(156.09, 286.7) * mm});
            skLineSegment(sketch, "E134.1.10", {"start": v(156.09, 286.7) * mm, "end": v(153.7, 282.58) * mm});
            skLineSegment(sketch, "E134.1.11", {"start": v(153.7, 282.58) * mm, "end": v(49.5, 342.74) * mm});
            skLineSegment(sketch, "E134.1.12", {"start": v(49.5, 342.74) * mm, "end": v(51.87, 346.87) * mm});
            skLineSegment(sketch, "E134.1.13", {"start": v(51.87, 346.87) * mm, "end": v(35.38, 356.4) * mm});
            skLineSegment(sketch, "E134.1.14", {"start": v(35.38, 356.4) * mm, "end": v(33, 352.27) * mm});
            skLineSegment(sketch, "E134.1.15", {"start": v(33, 352.27) * mm, "end": v(0, 371.32) * mm});
            skLineSegment(sketch, "E134.1.16", {"start": v(0, 371.32) * mm, "end": v(-33, 352.27) * mm});
            skLineSegment(sketch, "E134.1.17", {"start": v(-33, 352.27) * mm, "end": v(-35.38, 356.4) * mm});
            skLineSegment(sketch, "E134.1.18", {"start": v(-35.38, 356.4) * mm, "end": v(-51.87, 346.87) * mm});
            skLineSegment(sketch, "E134.1.19", {"start": v(-51.87, 346.87) * mm, "end": v(-49.5, 342.74) * mm});
            skLineSegment(sketch, "E134.1.20", {"start": v(-49.5, 342.74) * mm, "end": v(-153.7, 282.58) * mm});
            skLineSegment(sketch, "E134.1.21", {"start": v(-153.7, 282.58) * mm, "end": v(-156.09, 286.7) * mm});
            skLineSegment(sketch, "E134.1.22", {"start": v(-156.09, 286.7) * mm, "end": v(-172.59, 277.17) * mm});
            skLineSegment(sketch, "E134.1.23", {"start": v(-172.59, 277.17) * mm, "end": v(-170.2, 273.05) * mm});
            skLineSegment(sketch, "E134.1.24", {"start": v(-170.2, 273.05) * mm, "end": v(-203.2, 254) * mm});
            skLineSegment(sketch, "E134.1.25", {"start": v(-203.2, 254) * mm, "end": v(-203.2, 229) * mm});
            skLineSegment(sketch, "E134.1.26", {"start": v(-203.2, 229) * mm, "end": v(-198.04, 229) * mm});
            skLineSegment(sketch, "E134.1.27", {"start": v(-198.04, 229) * mm, "end": v(-198.04, 212.33) * mm});
            skLineSegment(sketch, "E134.1.28", {"start": v(-198.04, 212.33) * mm, "end": v(-203.2, 212.33) * mm});
            skLineSegment(sketch, "E134.1.29", {"start": v(-203.2, 212.33) * mm, "end": v(-203.2, 41.67) * mm});
            skLineSegment(sketch, "E134.1.30", {"start": v(-203.2, 41.67) * mm, "end": v(-198.04, 41.67) * mm});
            skLineSegment(sketch, "E134.1.31", {"start": v(-198.04, 41.67) * mm, "end": v(-198.04, 25) * mm});
            skLineSegment(sketch, "E134.1.32", {"start": v(-198.04, 25) * mm, "end": v(-203.2, 25) * mm});
            skLineSegment(sketch, "E134.1.33", {"start": v(-203.2, 25) * mm, "end": v(-203.2, 0) * mm});
            skLineSegment(sketch, "E134.1.34", {"start": v(-203.2, 0) * mm, "end": v(-25.4, 0) * mm});
            skLineSegment(sketch, "E134.1.35", {"start": v(-25.4, 0) * mm, "end": v(-25.4, 101.6) * mm});
            skLineSegment(sketch, "E134.1.36", {"start": v(-25.4, 101.6) * mm, "end": v(25.4, 101.6) * mm});
            skLineSegment(sketch, "E134.1.37", {"start": v(25.4, 101.6) * mm, "end": v(25.4, 0) * mm});
            skLineSegment(sketch, "E134.1.38", {"start": v(25.4, 0) * mm, "end": v(203.2, 0) * mm});
            skLineSegment(sketch, "E134.1.39", {"start": v(203.2, 0) * mm, "end": v(203.2, 25) * mm});
            skLineSegment(sketch, "E134.1.40", {"start": v(203.2, 25) * mm, "end": v(198.04, 25) * mm});
            skPoint(sketch, "E134.2", {"position": v(200.62, 25) * mm});
            skLineSegment(sketch, "E135", {"start": v(-203.2, 212.33) * mm, "end": v(-203.2, 229) * mm});
            skLineSegment(sketch, "E136", {"start": v(-203.2, 25) * mm, "end": v(-203.2, 41.67) * mm});
            skLineSegment(sketch, "E137", {"start": v(203.2, 212.33) * mm, "end": v(203.2, 229) * mm});
            skLineSegment(sketch, "E138", {"start": v(203.2, 25) * mm, "end": v(203.2, 41.67) * mm});
            skSolve(sketch);
        }
        {
            var Q0;
            Q0 = qSketchRegion(id + "F28", true);
            extrude(context, id + "F29", {"entities" : qUnion([Q0]), "operationType" : NewBodyOperationType.REMOVE, "endBound" : BoundingType.THROUGH_ALL, "oppositeDirection" : true, "depth" : 25.4 * mm, "offsetDistance" : 25.4 * mm});
        }
    });
